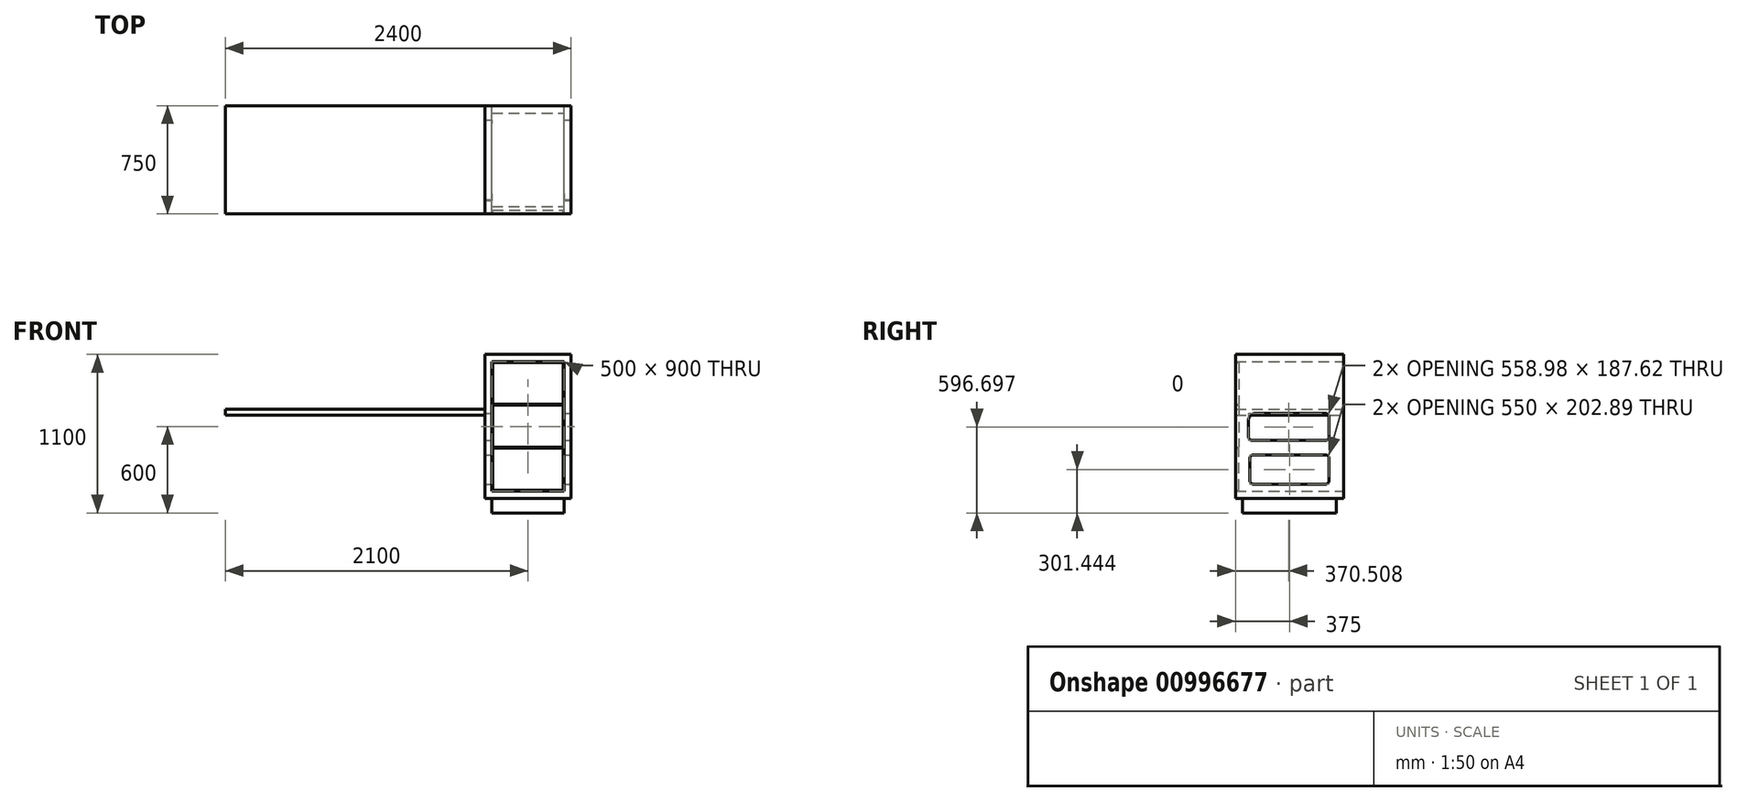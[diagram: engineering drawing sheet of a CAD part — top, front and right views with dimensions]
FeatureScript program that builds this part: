
annotation { "Feature Type Name" : "Feature", "Feature Type Description" : "" }
export const myFeature = defineFeature(function(context is Context, id is Id, definition is map)
    precondition{}
    {
        {
            assignVariable(context, id + "F0", {"name" : "t_depth", "anyValue" : 750});
        }
        {
            var Q0;
            Q0=qCreatedBy(makeId("Front.planeOp"),FACE);
            var sketch = newSketch(context, id + "F1", { "sketchPlane" : qUnion([Q0])});
            skLineSegment(sketch, "E0.bottom", {"start": v(-1265, 2470) * mm, "end": v(1265, 2470) * mm});
            skLineSegment(sketch, "E0.top", {"start": v(-1265, 0) * mm, "end": v(1265, 0) * mm});
            skLineSegment(sketch, "E0.left", {"start": v(-1265, 2470) * mm, "end": v(-1265, 0) * mm});
            skLineSegment(sketch, "E0.right", {"start": v(1265, 2470) * mm, "end": v(1265, 0) * mm});
            skSolve(sketch);
        }
        {
            var Q0;
            Q0=makeQuery(id+"F1.imprint","IMPRINT",FACE,{"disambiguationData":[TD([[makeQuery(id+"F1.imprint","IMPRINT",EDGE,{"derivedFrom":sQuery(id+"F1.wireOp",EDGE,"E0.bottom")}),-1.0]])]});
            var sketch = newSketch(context, id + "F2", { "sketchPlane" : qUnion([Q0])});
            skLineSegment(sketch, "E1.bottom", {"start": v(-1265, 720) * mm, "end": v(535, 720) * mm});
            skLineSegment(sketch, "E1.top", {"start": v(-1265, 680) * mm, "end": v(535, 680) * mm});
            skLineSegment(sketch, "E1.left", {"start": v(-1265, 720) * mm, "end": v(-1265, 680) * mm});
            skLineSegment(sketch, "E1.right", {"start": v(535, 720) * mm, "end": v(535, 680) * mm});
            skSolve(sketch);
        }
        {
            var Q0;
            Q0=makeQuery(id+"F1.imprint","IMPRINT",FACE,{"disambiguationData":[TD([[makeQuery(id+"F1.imprint","IMPRINT",EDGE,{"derivedFrom":sQuery(id+"F1.wireOp",EDGE,"E0.bottom")}),-1.0]])]});
            var sketch = newSketch(context, id + "F3", { "sketchPlane" : qUnion([Q0])});
            skLineSegment(sketch, "E2.bottom", {"start": v(-1265, 690) * mm, "end": v(535, 690) * mm});
            skLineSegment(sketch, "E2.top", {"start": v(-1265, 680) * mm, "end": v(535, 680) * mm});
            skLineSegment(sketch, "E2.left", {"start": v(-1265, 690) * mm, "end": v(-1265, 680) * mm});
            skLineSegment(sketch, "E2.right", {"start": v(535, 690) * mm, "end": v(535, 680) * mm});
            skSolve(sketch);
        }
        {
            var Q0;
            Q0=qSketchRegion(id+"F2",true);
            var Q1;
            Q1=qConstructionFilter(qBodyType(qCreatedBy(id+"F2",EDGE),BodyType.WIRE),ConstructionObject.NO);
            extrude(context, id + "F4", {"entities" : qUnion([Q0]), "surfaceEntities" : qUnion([Q1]), "depth" : (getVariable(context, 't_depth')) * mm, "offsetDistance" : 25 * mm});
        }
        {
            var Q0;
            Q0=makeQuery(id+"F1.imprint","IMPRINT",FACE,{"disambiguationData":[TD([[makeQuery(id+"F1.imprint","IMPRINT",EDGE,{"derivedFrom":sQuery(id+"F1.wireOp",EDGE,"E0.bottom")}),-1.0]])]});
            var sketch = newSketch(context, id + "F5", { "sketchPlane" : qUnion([Q0])});
            skLineSegment(sketch, "E3.bottom", {"start": v(535, 1000) * mm, "end": v(1135, 1000) * mm});
            skLineSegment(sketch, "E3.top", {"start": v(535, 0) * mm, "end": v(1135, 0) * mm});
            skLineSegment(sketch, "E3.left", {"start": v(535, 1000) * mm, "end": v(535, 0) * mm});
            skLineSegment(sketch, "E3.right", {"start": v(1135, 1000) * mm, "end": v(1135, 0) * mm});
            skSolve(sketch);
        }
        {
            var Q0;
            Q0=makeQuery(id+"F5.imprint","IMPRINT",FACE,{"disambiguationData":[TD([[makeQuery(id+"F5.imprint","IMPRINT",EDGE,{"derivedFrom":sQuery(id+"F5.wireOp",EDGE,"E3.bottom")}),-1.0]])]});
            extrude(context, id + "F6", {"entities" : qUnion([Q0]), "depth" : (getVariable(context, 't_depth')) * mm, "offsetDistance" : 25 * mm});
        }
        {
            var Q0;
            Q0=makeQuery(id+"F1.imprint","IMPRINT",FACE,{"disambiguationData":[TD([[makeQuery(id+"F1.imprint","IMPRINT",EDGE,{"derivedFrom":sQuery(id+"F1.wireOp",EDGE,"E0.bottom")}),-1.0]])]});
            var sketch = newSketch(context, id + "F7", { "sketchPlane" : qUnion([Q0])});
            skLineSegment(sketch, "E4.bottom", {"start": v(585, 950) * mm, "end": v(1085, 950) * mm});
            skLineSegment(sketch, "E4.top", {"start": v(585, 50) * mm, "end": v(1085, 50) * mm});
            skLineSegment(sketch, "E4.left", {"start": v(585, 950) * mm, "end": v(585, 50) * mm});
            skLineSegment(sketch, "E4.right", {"start": v(1085, 950) * mm, "end": v(1085, 50) * mm});
            skSolve(sketch);
        }
        {
            var Q0;
            Q0 = qSketchRegion(id + "F7", true);
            extrude(context, id + "F8", {"entities" : qUnion([Q0]), "operationType" : NewBodyOperationType.REMOVE, "endBound" : BoundingType.THROUGH_ALL, "depth" : 25 * mm, "offsetDistance" : 25 * mm});
        }
        {
            var Q0;
            Q0=makeQuery(id+"F6.opExtrude","SWEPT_FACE",FACE,{"disambiguationData":[OSD([sQuery(id+"F5.wireOp",EDGE,"E3.right")])]});
            var sketch = newSketch(context, id + "F9", { "sketchPlane" : qUnion([Q0])});
            skLineSegment(sketch, "E5.bottom", {"start": v(-625, 302.89) * mm, "end": v(-125, 302.89) * mm});
            skLineSegment(sketch, "E5.top", {"start": v(-625, 100) * mm, "end": v(-125, 100) * mm});
            skLineSegment(sketch, "E5.left", {"start": v(-650, 277.89) * mm, "end": v(-650, 125) * mm});
            skLineSegment(sketch, "E5.right", {"start": v(-100, 277.89) * mm, "end": v(-100, 125) * mm});
            skLineSegment(sketch, "E6.bottom", {"start": v(-608.98, 590.5) * mm, "end": v(-125, 590.5) * mm});
            skLineSegment(sketch, "E6.top", {"start": v(-633.98, 402.89) * mm, "end": v(-125, 402.89) * mm});
            skLineSegment(sketch, "E6.left", {"start": v(-658.98, 540.5) * mm, "end": v(-658.98, 427.89) * mm});
            skLineSegment(sketch, "E6.right", {"start": v(-100, 565.5) * mm, "end": v(-100, 427.89) * mm});
            skPoint(sketch, "E7.visualSharp", {"position": v(-658.98, 590.5) * mm});
            skArc(sketch, "E7.filletArc", {"start": v(-633.98, 590.5) * mm, "mid": v(-651.66, 583.18) * mm, "end": v(-658.98, 565.5) * mm});
            skPoint(sketch, "E8.visualSharp", {"position": v(-100, 402.89) * mm});
            skArc(sketch, "E8.filletArc", {"start": v(-125, 402.89) * mm, "mid": v(-107.32, 410.2) * mm, "end": v(-100, 427.89) * mm});
            skPoint(sketch, "E9.visualSharp", {"position": v(-100, 590.5) * mm});
            skArc(sketch, "E9.filletArc", {"start": v(-100, 565.5) * mm, "mid": v(-107.32, 583.18) * mm, "end": v(-125, 590.5) * mm});
            skPoint(sketch, "E10.visualSharp", {"position": v(-658.98, 402.89) * mm});
            skArc(sketch, "E10.filletArc", {"start": v(-658.98, 427.89) * mm, "mid": v(-651.66, 410.2) * mm, "end": v(-633.98, 402.89) * mm});
            skArc(sketch, "E11.filletArc", {"start": v(-608.98, 590.5) * mm, "mid": v(-644.34, 575.86) * mm, "end": v(-658.98, 540.5) * mm});
            skPoint(sketch, "E12.visualSharp", {"position": v(-650, 302.89) * mm});
            skArc(sketch, "E12.filletArc", {"start": v(-625, 302.89) * mm, "mid": v(-642.68, 295.57) * mm, "end": v(-650, 277.89) * mm});
            skPoint(sketch, "E13.visualSharp", {"position": v(-100, 302.89) * mm});
            skArc(sketch, "E13.filletArc", {"start": v(-100, 277.89) * mm, "mid": v(-107.32, 295.57) * mm, "end": v(-125, 302.89) * mm});
            skPoint(sketch, "E14.visualSharp", {"position": v(-650, 100) * mm});
            skArc(sketch, "E14.filletArc", {"start": v(-650, 125) * mm, "mid": v(-642.68, 107.32) * mm, "end": v(-625, 100) * mm});
            skPoint(sketch, "E15.visualSharp", {"position": v(-100, 100) * mm});
            skArc(sketch, "E15.filletArc", {"start": v(-125, 100) * mm, "mid": v(-107.32, 107.32) * mm, "end": v(-100, 125) * mm});
            skSolve(sketch);
        }
        {
            var Q0;
            Q0=makeQuery(id+"F9.imprint","IMPRINT",FACE,{"disambiguationData":[TD([[makeQuery(id+"F9.imprint","IMPRINT",EDGE,{"derivedFrom":sQuery(id+"F9.wireOp",EDGE,"E6.bottom")}),-1.0]])]});
            var Q1;
            Q1=makeQuery(id+"F9.imprint","IMPRINT",FACE,{"disambiguationData":[TD([[makeQuery(id+"F9.imprint","IMPRINT",EDGE,{"derivedFrom":sQuery(id+"F9.wireOp",EDGE,"E5.bottom")}),-1.0]])]});
            extrude(context, id + "F10", {"entities" : qUnion([Q0, Q1]), "operationType" : NewBodyOperationType.REMOVE, "endBound" : BoundingType.THROUGH_ALL, "oppositeDirection" : true, "depth" : 25 * mm, "offsetDistance" : 25 * mm});
        }
        {
            var Q0;
            Q0=makeQuery(id+"F1.imprint","IMPRINT",FACE,{"disambiguationData":[TD([[makeQuery(id+"F1.imprint","IMPRINT",EDGE,{"derivedFrom":sQuery(id+"F1.wireOp",EDGE,"E0.bottom")}),-1.0]])]});
            var sketch = newSketch(context, id + "F11", { "sketchPlane" : qUnion([Q0])});
            skLineSegment(sketch, "E16.bottom", {"start": v(590, 945) * mm, "end": v(1080, 945) * mm});
            skLineSegment(sketch, "E16.top", {"start": v(590, 653.33) * mm, "end": v(1080, 653.33) * mm});
            skLineSegment(sketch, "E16.left", {"start": v(1080, 945) * mm, "end": v(1080, 653.33) * mm});
            skLineSegment(sketch, "E16.right", {"start": v(590, 945) * mm, "end": v(590, 653.33) * mm});
            skPoint(sketch, "E17.oppositeSnap0", {"position": v(590, 799.17) * mm});
            skLineSegment(sketch, "E18.bottom", {"start": v(590, 647.16) * mm, "end": v(1080, 647.16) * mm});
            skLineSegment(sketch, "E18.top", {"start": v(590, 355.5) * mm, "end": v(1080, 355.5) * mm});
            skLineSegment(sketch, "E18.left", {"start": v(590, 647.16) * mm, "end": v(590, 355.5) * mm});
            skLineSegment(sketch, "E18.right", {"start": v(1080, 647.16) * mm, "end": v(1080, 355.5) * mm});
            skLineSegment(sketch, "E19.bottom", {"start": v(590, 58.68) * mm, "end": v(1080, 58.68) * mm});
            skLineSegment(sketch, "E19.top", {"start": v(590, 350.35) * mm, "end": v(1080, 350.35) * mm});
            skLineSegment(sketch, "E19.left", {"start": v(590, 58.68) * mm, "end": v(590, 350.35) * mm});
            skLineSegment(sketch, "E19.right", {"start": v(1080, 58.68) * mm, "end": v(1080, 350.35) * mm});
            skSolve(sketch);
        }
        {
            var Q0;
            Q0=makeQuery(id+"F11.imprint","IMPRINT",FACE,{"disambiguationData":[TD([[makeQuery(id+"F11.imprint","IMPRINT",EDGE,{"derivedFrom":sQuery(id+"F11.wireOp",EDGE,"E18.bottom")}),-1.0]])]});
            var Q1;
            Q1=makeQuery(id+"F11.imprint","IMPRINT",FACE,{"disambiguationData":[TD([[makeQuery(id+"F11.imprint","IMPRINT",EDGE,{"derivedFrom":sQuery(id+"F11.wireOp",EDGE,"E16.bottom")}),-1.0]])]});
            var Q2;
            Q2=makeQuery(id+"F11.imprint","IMPRINT",FACE,{"disambiguationData":[TD([[makeQuery(id+"F11.imprint","IMPRINT",EDGE,{"derivedFrom":sQuery(id+"F11.wireOp",EDGE,"E19.bottom")}),1.0]])]});
            extrude(context, id + "F12", {"entities" : qUnion([Q0, Q1, Q2]), "depth" : 25 * mm, "offsetDistance" : 25 * mm});
        }
        {
            var Q0;
            Q0=makeQuery(id+"F12.opExtrude","SWEPT_BODY",BODY,{"disambiguationData":[OSD([sQuery(id+"F11.wireOp",EDGE,"E16.bottom"),sQuery(id+"F11.wireOp",EDGE,"E16.top"),sQuery(id+"F11.wireOp",EDGE,"E16.left"),sQuery(id+"F11.wireOp",EDGE,"E16.right")])]});
            var Q1;
            Q1=makeQuery(id+"F12.opExtrude","SWEPT_BODY",BODY,{"disambiguationData":[OSD([sQuery(id+"F11.wireOp",EDGE,"E18.bottom"),sQuery(id+"F11.wireOp",EDGE,"E18.top"),sQuery(id+"F11.wireOp",EDGE,"E18.left"),sQuery(id+"F11.wireOp",EDGE,"E18.right")])]});
            var Q2;
            Q2=makeQuery(id+"F12.opExtrude","SWEPT_BODY",BODY,{"disambiguationData":[OSD([sQuery(id+"F11.wireOp",EDGE,"E19.bottom"),sQuery(id+"F11.wireOp",EDGE,"E19.top"),sQuery(id+"F11.wireOp",EDGE,"E19.left"),sQuery(id+"F11.wireOp",EDGE,"E19.right")])]});
            transform(context, id + "F13", {"entities" : qUnion([Q0, Q1, Q2]), "transformType" : TransformType.TRANSLATION_3D, "dx" : 0 * mm, "dy" : -(getVariable(context, 't_depth') - 25) * mm, "dz" : 0 * mm, "makeCopy" : false});
        }
        {
            var Q0;
            Q0=makeQuery(id+"F6.opExtrude","SWEPT_BODY",BODY,{"disambiguationData":[OSD([sQuery(id+"F5.wireOp",EDGE,"E3.bottom"),sQuery(id+"F5.wireOp",EDGE,"E3.top"),sQuery(id+"F5.wireOp",EDGE,"E3.left"),sQuery(id+"F5.wireOp",EDGE,"E3.right")])]});
            var Q1;
            Q1=makeQuery(id+"F12.opExtrude","SWEPT_BODY",BODY,{"disambiguationData":[OSD([sQuery(id+"F11.wireOp",EDGE,"E16.bottom"),sQuery(id+"F11.wireOp",EDGE,"E16.top"),sQuery(id+"F11.wireOp",EDGE,"E16.left"),sQuery(id+"F11.wireOp",EDGE,"E16.right")])]});
            var Q2;
            Q2=makeQuery(id+"F12.opExtrude","SWEPT_BODY",BODY,{"disambiguationData":[OSD([sQuery(id+"F11.wireOp",EDGE,"E18.bottom"),sQuery(id+"F11.wireOp",EDGE,"E18.top"),sQuery(id+"F11.wireOp",EDGE,"E18.left"),sQuery(id+"F11.wireOp",EDGE,"E18.right")])]});
            var Q3;
            Q3=makeQuery(id+"F12.opExtrude","SWEPT_BODY",BODY,{"disambiguationData":[OSD([sQuery(id+"F11.wireOp",EDGE,"E19.bottom"),sQuery(id+"F11.wireOp",EDGE,"E19.top"),sQuery(id+"F11.wireOp",EDGE,"E19.left"),sQuery(id+"F11.wireOp",EDGE,"E19.right")])]});
            transform(context, id + "F14", {"entities" : qUnion([Q0, Q1, Q2, Q3]), "transformType" : TransformType.TRANSLATION_3D, "dx" : 0 * mm, "dy" : 0 * mm, "dz" : 100 * mm, "makeCopy" : false});
        }
        {
            var Q0;
            Q0=makeQuery(id+"F6.opExtrude","SWEPT_FACE",FACE,{"disambiguationData":[OSD([sQuery(id+"F5.wireOp",EDGE,"E3.top")])]});
            var sketch = newSketch(context, id + "F15", { "sketchPlane" : qUnion([Q0])});
            skLineSegment(sketch, "E20.bottom", {"start": v(585, 700) * mm, "end": v(1085, 700) * mm});
            skLineSegment(sketch, "E20.top", {"start": v(585, 50) * mm, "end": v(1085, 50) * mm});
            skLineSegment(sketch, "E20.left", {"start": v(585, 700) * mm, "end": v(585, 50) * mm});
            skLineSegment(sketch, "E20.right", {"start": v(1085, 700) * mm, "end": v(1085, 50) * mm});
            skSolve(sketch);
        }
        {
            var Q0;
            Q0=makeQuery(id+"F15.imprint","IMPRINT",FACE,{"disambiguationData":[TD([[makeQuery(id+"F15.imprint","IMPRINT",EDGE,{"derivedFrom":sQuery(id+"F15.wireOp",EDGE,"E20.bottom")}),-1.0]])]});
            extrude(context, id + "F16", {"entities" : qUnion([Q0]), "operationType" : NewBodyOperationType.ADD, "depth" : 100 * mm, "offsetDistance" : 25 * mm});
        }
    });
